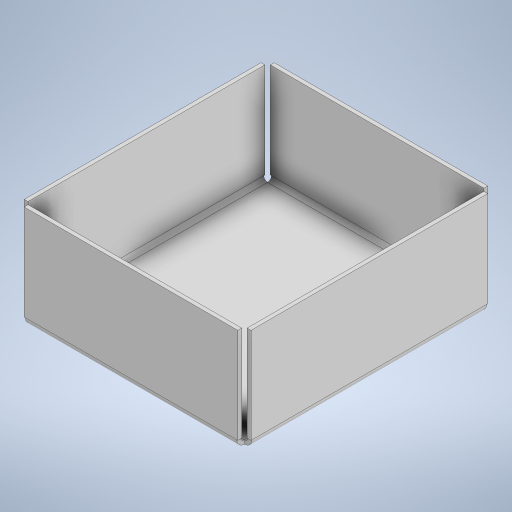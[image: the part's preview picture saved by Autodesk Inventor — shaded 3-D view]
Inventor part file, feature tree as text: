
AUTODESK INVENTOR PART (.ipt)
format: ipt  version: 2024.3 (Build 283343000, 343)  size: 291,840 bytes
history: native  units: mm
features: sheet_metal_op x4, other x3, sketch x2
ambient origin geometry x8: Origin, YZ Plane, XZ Plane, XY Plane, X Axis, Y Axis, Z Axis, Center Point
bodies: Solid1 (feature_tree)
feature tree (9):
  sheet_metal_op  "Face1"
  sheet_metal_op  "Flange1"
  sketch  "Sketch1"  dims[d0=97.0mm]
  other  "Plate1"
  sketch  "Sketch2"  dims[d1=88.0mm d2=1.5mm d3=1.5mm d4=0.75mm d5=3.0mm d6=1.5mm d7=40.0mm d8=90.0deg d9=1.5mm d10=6.0mm d11=1.5mm d12=1.5mm]
  other  "Plate2"
  sheet_metal_op  "Bend1"
  sheet_metal_op  "Corner1"
  other  "Definition1"
